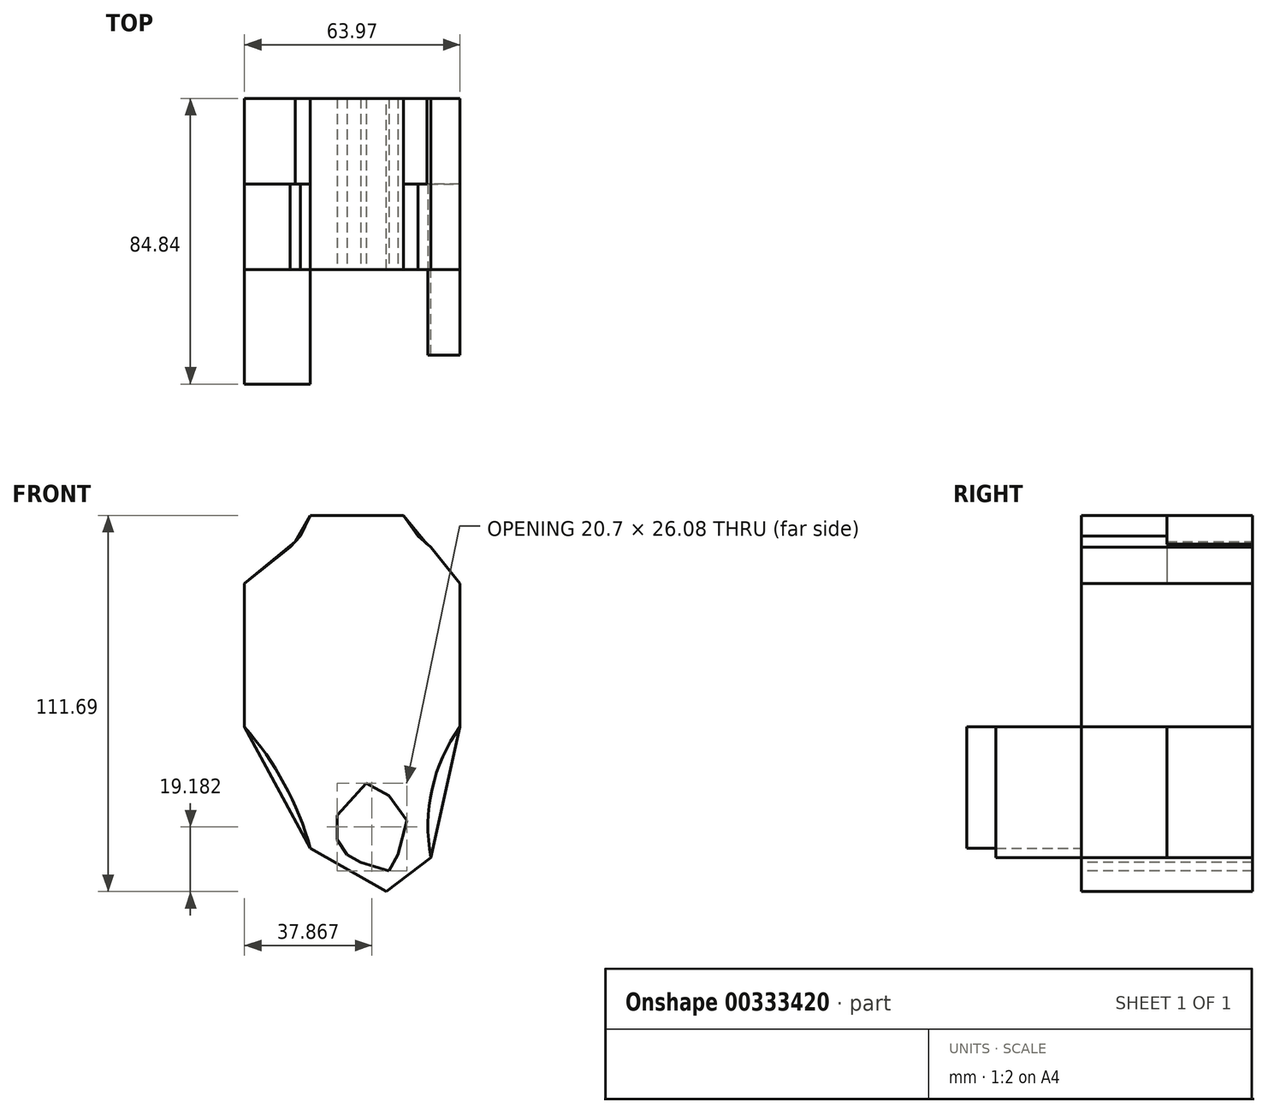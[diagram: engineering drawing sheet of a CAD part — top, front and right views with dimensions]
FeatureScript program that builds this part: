
annotation { "Feature Type Name" : "Feature", "Feature Type Description" : "" }
export const myFeature = defineFeature(function(context is Context, id is Id, definition is map)
    precondition{}
    {
        {
            var Q0;
            Q0=qCreatedBy(makeId("Front.planeOp"),FACE);
            var sketch = newSketch(context, id + "F0", { "sketchPlane" : qUnion([Q0])});
            skLineSegment(sketch, "E0", {"start": v(-51.56, 46.9) * mm, "end": v(-38.07, 57.69) * mm});
            skLineSegment(sketch, "E1", {"start": v(-35.03, 61.06) * mm, "end": v(-38.07, 57.69) * mm});
            skLineSegment(sketch, "E2", {"start": v(-35.03, 61.06) * mm, "end": v(-32, 67.14) * mm});
            skLineSegment(sketch, "E3", {"start": v(-32, 67.14) * mm, "end": v(-4.32, 67.14) * mm});
            skLineSegment(sketch, "E4", {"start": v(-4.32, 67.14) * mm, "end": v(0, 61.06) * mm});
            skLineSegment(sketch, "E5", {"start": v(0, 61.06) * mm, "end": v(3.77, 57.69) * mm});
            skLineSegment(sketch, "E6", {"start": v(3.77, 57.69) * mm, "end": v(12.41, 46.9) * mm});
            skLineSegment(sketch, "E7", {"start": v(12.41, 24.29) * mm, "end": v(12.41, 46.9) * mm});
            skLineSegment(sketch, "E8", {"start": v(12.41, 24.29) * mm, "end": v(12.41, 4.38) * mm});
            skLineSegment(sketch, "E9", {"start": v(12.41, 4.38) * mm, "end": v(3.77, -34.42) * mm});
            skLineSegment(sketch, "E10", {"start": v(-51.56, 46.9) * mm, "end": v(-51.56, 24.29) * mm});
            skLineSegment(sketch, "E11", {"start": v(-51.56, 4.38) * mm, "end": v(-51.56, 24.29) * mm});
            skLineSegment(sketch, "E12", {"start": v(-51.56, 4.38) * mm, "end": v(-32, -31.72) * mm});
            skLineSegment(sketch, "E13", {"start": v(-32, -31.72) * mm, "end": v(-9.39, -44.55) * mm});
            skLineSegment(sketch, "E14", {"start": v(3.77, -34.42) * mm, "end": v(-9.39, -44.55) * mm});
            skSolve(sketch);
        }
        {
            var Q0;
            Q0=makeQuery(id+"F0.imprint","IMPRINT",FACE,{"disambiguationData":[TD([[makeQuery(id+"F0.imprint","IMPRINT",EDGE,{"derivedFrom":sQuery(id+"F0.wireOp",EDGE,"E0")}),-1.0]])]});
            extrude(context, id + "F1", {"entities" : qUnion([Q0]), "depth" : 25.4 * mm});
        }
        {
            var Q0;
            Q0=makeQuery(id+"F1.opExtrude","CAP_FACE",FACE,{"disambiguationData":[OSD([sQuery(id+"F0.wireOp",EDGE,"E0"),sQuery(id+"F0.wireOp",EDGE,"E1"),sQuery(id+"F0.wireOp",EDGE,"E2"),sQuery(id+"F0.wireOp",EDGE,"E3"),sQuery(id+"F0.wireOp",EDGE,"E4"),sQuery(id+"F0.wireOp",EDGE,"E5"),sQuery(id+"F0.wireOp",EDGE,"E6"),sQuery(id+"F0.wireOp",EDGE,"E7"),sQuery(id+"F0.wireOp",EDGE,"E8"),sQuery(id+"F0.wireOp",EDGE,"E9"),sQuery(id+"F0.wireOp",EDGE,"E10"),sQuery(id+"F0.wireOp",EDGE,"E11"),sQuery(id+"F0.wireOp",EDGE,"E12"),sQuery(id+"F0.wireOp",EDGE,"E13"),sQuery(id+"F0.wireOp",EDGE,"E14")])],"isStart":true});
            extrude(context, id + "F2", {"entities" : qUnion([Q0]), "operationType" : NewBodyOperationType.ADD, "depth" : 25.4 * mm});
        }
        {
            var Q0;
            Q0=makeQuery(id+"F2.opExtrude","CAP_FACE",FACE,{"disambiguationData":[OSD([sQuery(id+"F0.wireOp",EDGE,"E0"),sQuery(id+"F0.wireOp",EDGE,"E1"),sQuery(id+"F0.wireOp",EDGE,"E2"),sQuery(id+"F0.wireOp",EDGE,"E3"),sQuery(id+"F0.wireOp",EDGE,"E4"),sQuery(id+"F0.wireOp",EDGE,"E5"),sQuery(id+"F0.wireOp",EDGE,"E6"),sQuery(id+"F0.wireOp",EDGE,"E7"),sQuery(id+"F0.wireOp",EDGE,"E8"),sQuery(id+"F0.wireOp",EDGE,"E9"),sQuery(id+"F0.wireOp",EDGE,"E10"),sQuery(id+"F0.wireOp",EDGE,"E11"),sQuery(id+"F0.wireOp",EDGE,"E12"),sQuery(id+"F0.wireOp",EDGE,"E13"),sQuery(id+"F0.wireOp",EDGE,"E14")])],"isStart":false});
            var sketch = newSketch(context, id + "F3", { "sketchPlane" : qUnion([Q0])});
            skLineSegment(sketch, "E15", {"start": v(4.32, 67.14) * mm, "end": v(-12.41, 46.9) * mm});
            skLineSegment(sketch, "E16", {"start": v(-12.41, 46.9) * mm, "end": v(-12.41, 4.38) * mm});
            skLineSegment(sketch, "E17", {"start": v(-12.41, 4.38) * mm, "end": v(-3.77, -34.42) * mm});
            skLineSegment(sketch, "E18", {"start": v(-3.77, -34.42) * mm, "end": v(9.39, -44.55) * mm});
            skLineSegment(sketch, "E19", {"start": v(9.39, -44.55) * mm, "end": v(32, -31.72) * mm});
            skLineSegment(sketch, "E20", {"start": v(32, -31.72) * mm, "end": v(51.56, 4.38) * mm});
            skLineSegment(sketch, "E21", {"start": v(51.56, 4.38) * mm, "end": v(51.56, 46.9) * mm});
            skLineSegment(sketch, "E22", {"start": v(51.07, 47.38) * mm, "end": v(35.03, 59.38) * mm});
            skPoint(sketch, "E22.endSnap0", {"position": v(36.55, 59.38) * mm});
            skLineSegment(sketch, "E23", {"start": v(36.55, 59.38) * mm, "end": v(32, 67.14) * mm});
            skLineSegment(sketch, "E24", {"start": v(32, 67.14) * mm, "end": v(18.16, 67.14) * mm});
            skLineSegment(sketch, "E25", {"start": v(36.55, 59.38) * mm, "end": v(51.56, 46.9) * mm});
            skLineSegment(sketch, "E26", {"start": v(4.32, 67.14) * mm, "end": v(32, 67.14) * mm});
            skSolve(sketch);
        }
        {
            var Q0;
            Q0=makeQuery(id+"F1.opExtrude","CAP_FACE",FACE,{"disambiguationData":[OSD([sQuery(id+"F0.wireOp",EDGE,"E0"),sQuery(id+"F0.wireOp",EDGE,"E1"),sQuery(id+"F0.wireOp",EDGE,"E2"),sQuery(id+"F0.wireOp",EDGE,"E3"),sQuery(id+"F0.wireOp",EDGE,"E4"),sQuery(id+"F0.wireOp",EDGE,"E5"),sQuery(id+"F0.wireOp",EDGE,"E6"),sQuery(id+"F0.wireOp",EDGE,"E7"),sQuery(id+"F0.wireOp",EDGE,"E8"),sQuery(id+"F0.wireOp",EDGE,"E9"),sQuery(id+"F0.wireOp",EDGE,"E10"),sQuery(id+"F0.wireOp",EDGE,"E11"),sQuery(id+"F0.wireOp",EDGE,"E12"),sQuery(id+"F0.wireOp",EDGE,"E13"),sQuery(id+"F0.wireOp",EDGE,"E14")])],"isStart":false});
            var sketch = newSketch(context, id + "F4", { "sketchPlane" : qUnion([Q0])});
            skArc(sketch, "E27", {"start": v(-32, -31.72) * mm, "mid": v(-37.53, -11.37) * mm, "end": v(-51.56, 4.38) * mm});
            skArc(sketch, "E28", {"start": v(12.41, 4.38) * mm, "mid": v(4.12, -14.14) * mm, "end": v(3.77, -34.42) * mm});
            skArc(sketch, "E29", {"start": v(-9.39, -44.55) * mm, "mid": v(-20.3, -37.44) * mm, "end": v(-32, -31.72) * mm});
            skArc(sketch, "E30", {"start": v(3.77, -34.42) * mm, "mid": v(-4.16, -37.73) * mm, "end": v(-9.39, -44.55) * mm});
            skLineSegment(sketch, "E31", {"start": v(3.77, -34.42) * mm, "end": v(12.41, 4.38) * mm});
            skSolve(sketch);
        }
        {
            var Q0;
            Q0=makeQuery(id+"F4.imprint","IMPRINT",FACE,{"disambiguationData":[TD([[makeQuery(id+"F4.imprint","IMPRINT",EDGE,{"derivedFrom":sQuery(id+"F4.wireOp",EDGE,"E28")}),1.0]])]});
            extrude(context, id + "F5", {"entities" : qUnion([Q0]), "operationType" : NewBodyOperationType.REMOVE, "oppositeDirection" : true, "depth" : 51.05 * mm});
        }
        {
            var Q0;
            Q0 = qSketchRegion(id + "F4", true);
            var Q1;
            Q1 = qSketchRegion(id + "F3", true);
            extrude(context, id + "F6", {"entities" : qUnion([Q0, Q1]), "operationType" : NewBodyOperationType.ADD, "depth" : 25.4 * mm});
        }
        {
            var Q0;
            Q0=makeQuery(id+"F1.opExtrude","CAP_FACE",FACE,{"disambiguationData":[OSD([sQuery(id+"F0.wireOp",EDGE,"E0"),sQuery(id+"F0.wireOp",EDGE,"E1"),sQuery(id+"F0.wireOp",EDGE,"E2"),sQuery(id+"F0.wireOp",EDGE,"E3"),sQuery(id+"F0.wireOp",EDGE,"E4"),sQuery(id+"F0.wireOp",EDGE,"E5"),sQuery(id+"F0.wireOp",EDGE,"E6"),sQuery(id+"F0.wireOp",EDGE,"E7"),sQuery(id+"F0.wireOp",EDGE,"E8"),sQuery(id+"F0.wireOp",EDGE,"E9"),sQuery(id+"F0.wireOp",EDGE,"E10"),sQuery(id+"F0.wireOp",EDGE,"E11"),sQuery(id+"F0.wireOp",EDGE,"E12"),sQuery(id+"F0.wireOp",EDGE,"E13"),sQuery(id+"F0.wireOp",EDGE,"E14")])],"isStart":false});
            var sketch = newSketch(context, id + "F7", { "sketchPlane" : qUnion([Q0])});
            skArc(sketch, "E32", {"start": v(-32, -31.72) * mm, "mid": v(-39.74, -12.57) * mm, "end": v(-51.56, 4.38) * mm});
            skSolve(sketch);
        }
        {
            var Q0;
            Q0=makeQuery(id+"F7.imprint","IMPRINT",FACE,{"disambiguationData":[TD([[makeQuery(id+"F7.imprint","IMPRINT",EDGE,{"derivedFrom":sQuery(id+"F7.wireOp",EDGE,"E32")}),1.0]])]});
            extrude(context, id + "F8", {"entities" : qUnion([Q0]), "operationType" : NewBodyOperationType.ADD, "depth" : 25.15 * mm});
        }
        {
            var Q0;
            Q0=makeQuery(id+"F8.opExtrude","CAP_FACE",FACE,{"disambiguationData":[OSD([sQuery(id+"F0.wireOp",EDGE,"E12"),sQuery(id+"F7.wireOp",EDGE,"E32")])],"isStart":false});
            extrude(context, id + "F9", {"entities" : qUnion([Q0]), "operationType" : NewBodyOperationType.ADD, "depth" : 8.9 * mm});
        }
        {
            var Q0;
            Q0=makeQuery(id+"F1.opExtrude","CAP_FACE",FACE,{"disambiguationData":[OSD([sQuery(id+"F0.wireOp",EDGE,"E0"),sQuery(id+"F0.wireOp",EDGE,"E1"),sQuery(id+"F0.wireOp",EDGE,"E2"),sQuery(id+"F0.wireOp",EDGE,"E3"),sQuery(id+"F0.wireOp",EDGE,"E4"),sQuery(id+"F0.wireOp",EDGE,"E5"),sQuery(id+"F0.wireOp",EDGE,"E6"),sQuery(id+"F0.wireOp",EDGE,"E7"),sQuery(id+"F0.wireOp",EDGE,"E8"),sQuery(id+"F0.wireOp",EDGE,"E9"),sQuery(id+"F0.wireOp",EDGE,"E10"),sQuery(id+"F0.wireOp",EDGE,"E11"),sQuery(id+"F0.wireOp",EDGE,"E12"),sQuery(id+"F0.wireOp",EDGE,"E13"),sQuery(id+"F0.wireOp",EDGE,"E14")])],"isStart":false});
            var sketch = newSketch(context, id + "F10", { "sketchPlane" : qUnion([Q0])});
            skLineSegment(sketch, "E33", {"start": v(-24.04, -21.88) * mm, "end": v(-24.04, -29.2) * mm});
            skLineSegment(sketch, "E34", {"start": v(-24.04, -29.2) * mm, "end": v(-21.08, -33.58) * mm});
            skLineSegment(sketch, "E35", {"start": v(-21.08, -33.58) * mm, "end": v(-17.05, -35.84) * mm});
            skLineSegment(sketch, "E36", {"start": v(-17.05, -35.84) * mm, "end": v(-8.65, -38.41) * mm});
            skLineSegment(sketch, "E37", {"start": v(-8.65, -38.41) * mm, "end": v(-6.01, -33.58) * mm});
            skLineSegment(sketch, "E38", {"start": v(-6.01, -33.58) * mm, "end": v(-3.34, -23.37) * mm});
            skLineSegment(sketch, "E39", {"start": v(-3.34, -23.37) * mm, "end": v(-8.65, -16.11) * mm});
            skLineSegment(sketch, "E40", {"start": v(-8.65, -16.11) * mm, "end": v(-17.05, -11.44) * mm});
            skLineSegment(sketch, "E41", {"start": v(-24.04, -21.88) * mm, "end": v(-15.46, -12.33) * mm});
            skLineSegment(sketch, "E42", {"start": v(-17.05, -11.44) * mm, "end": v(-19.66, -16.11) * mm});
            skCircle(sketch, "E43", {"center": v(-10.04, -35.6) * mm, "radius": 2.28 * mm});
            skSolve(sketch);
        }
        {
            var Q0;
            Q0 = qSketchRegion(id + "F10", true);
            extrude(context, id + "F11", {"entities" : qUnion([Q0]), "operationType" : NewBodyOperationType.ADD, "depth" : 25.4 * mm});
        }
        {
            var Q0;
            Q0=makeQuery(id+"F11.opExtrude","CAP_FACE",FACE,{"disambiguationData":[OSD([sQuery(id+"F10.wireOp",EDGE,"E33"),sQuery(id+"F10.wireOp",EDGE,"E34"),sQuery(id+"F10.wireOp",EDGE,"E35"),sQuery(id+"F10.wireOp",EDGE,"E36"),sQuery(id+"F10.wireOp",EDGE,"E37"),sQuery(id+"F10.wireOp",EDGE,"E38"),sQuery(id+"F10.wireOp",EDGE,"E39"),sQuery(id+"F10.wireOp",EDGE,"E40"),sQuery(id+"F10.wireOp",EDGE,"E41")])],"isStart":false});
            extrude(context, id + "F12", {"entities" : qUnion([Q0]), "operationType" : NewBodyOperationType.REMOVE, "oppositeDirection" : true, "depth" : 81.8 * mm});
        }
    });
